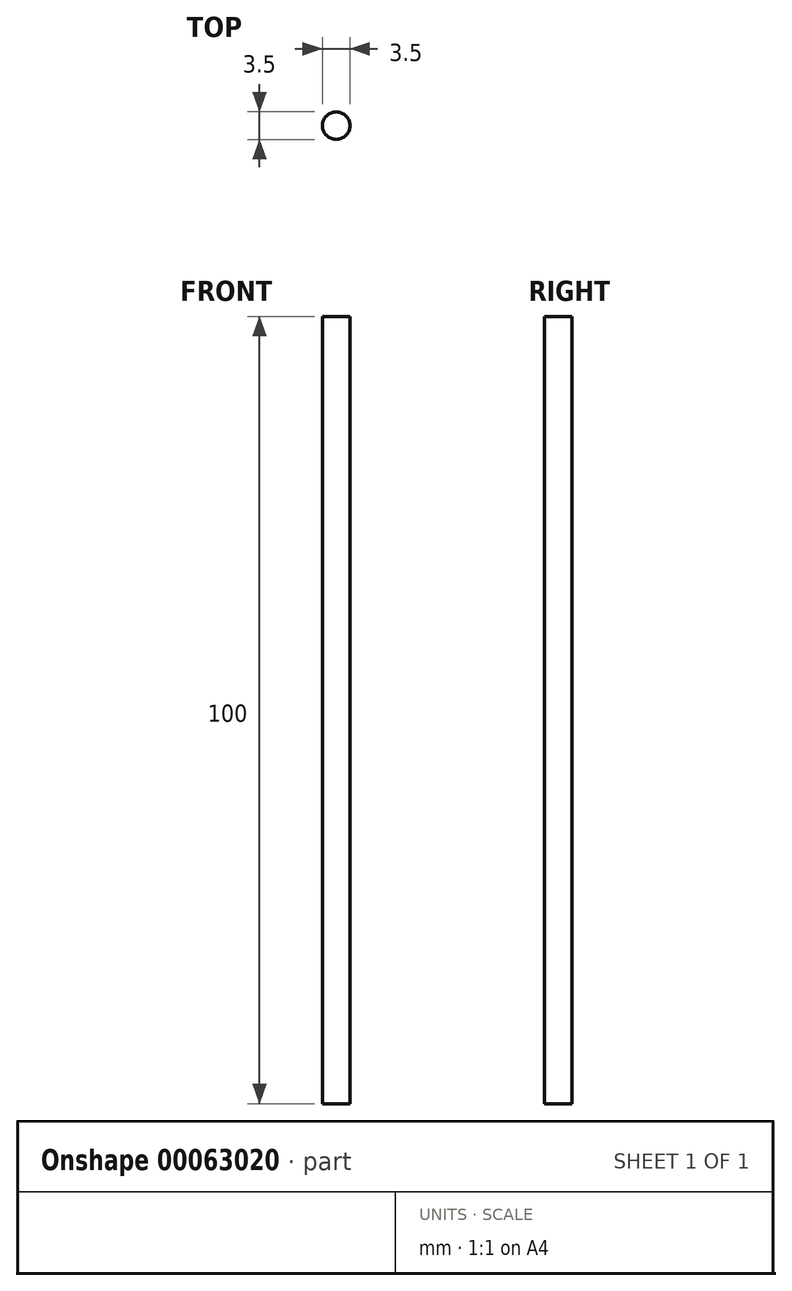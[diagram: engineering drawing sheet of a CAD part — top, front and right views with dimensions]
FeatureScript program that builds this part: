
annotation { "Feature Type Name" : "Feature", "Feature Type Description" : "" }
export const myFeature = defineFeature(function(context is Context, id is Id, definition is map)
    precondition{}
    {
        {
            var Q0;
            Q0=qCreatedBy(makeId("Top.planeOp"),FACE);
            var sketch = newSketch(context, id + "F0", { "sketchPlane" : qUnion([Q0])});
            skCircle(sketch, "E0", {"center": v(0, 0) * mm, "radius": 1.75 * mm});
            skSolve(sketch);
        }
        {
            var Q0;
            Q0=makeQuery(id+"F0.imprint","IMPRINT",FACE,{"disambiguationData":[TD([[makeQuery(id+"F0.imprint","IMPRINT",EDGE,{"derivedFrom":sQuery(id+"F0.wireOp",EDGE,"E0")}),1.0]])]});
            extrude(context, id + "F1", {"entities" : qUnion([Q0]), "depth" : 100 * mm});
        }
    });
